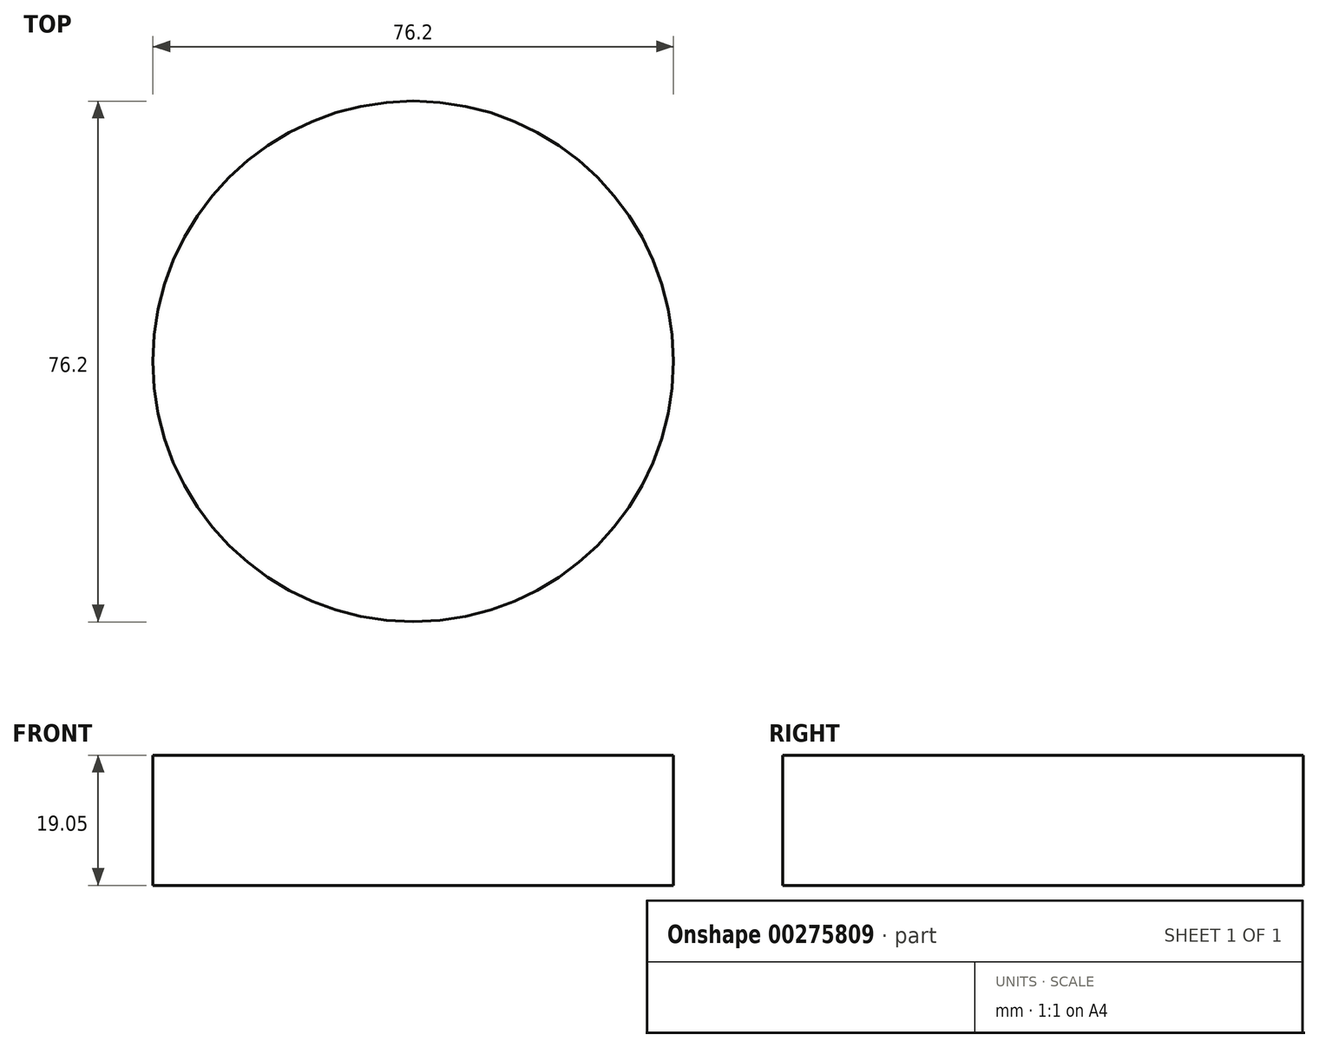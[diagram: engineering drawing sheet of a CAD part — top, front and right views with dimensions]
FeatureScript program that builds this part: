
annotation { "Feature Type Name" : "Feature", "Feature Type Description" : "" }
export const myFeature = defineFeature(function(context is Context, id is Id, definition is map)
    precondition{}
    {
        {
            var Q0;
            Q0=qCreatedBy(makeId("Top.planeOp"),FACE);
            var sketch = newSketch(context, id + "F0", { "sketchPlane" : qUnion([Q0])});
            skCircle(sketch, "E0", {"center": v(-47.32, -29.72) * mm, "radius": 38.1 * mm});
            skSolve(sketch);
        }
        {
            var Q0;
            Q0=makeQuery(id+"F0.imprint","IMPRINT",FACE,{"disambiguationData":[TD([[makeQuery(id+"F0.imprint","IMPRINT",EDGE,{"derivedFrom":sQuery(id+"F0.wireOp",EDGE,"E0")}),1.0]])]});
            extrude(context, id + "F1", {"entities" : qUnion([Q0]), "depth" : 19.05 * mm});
        }
    });
